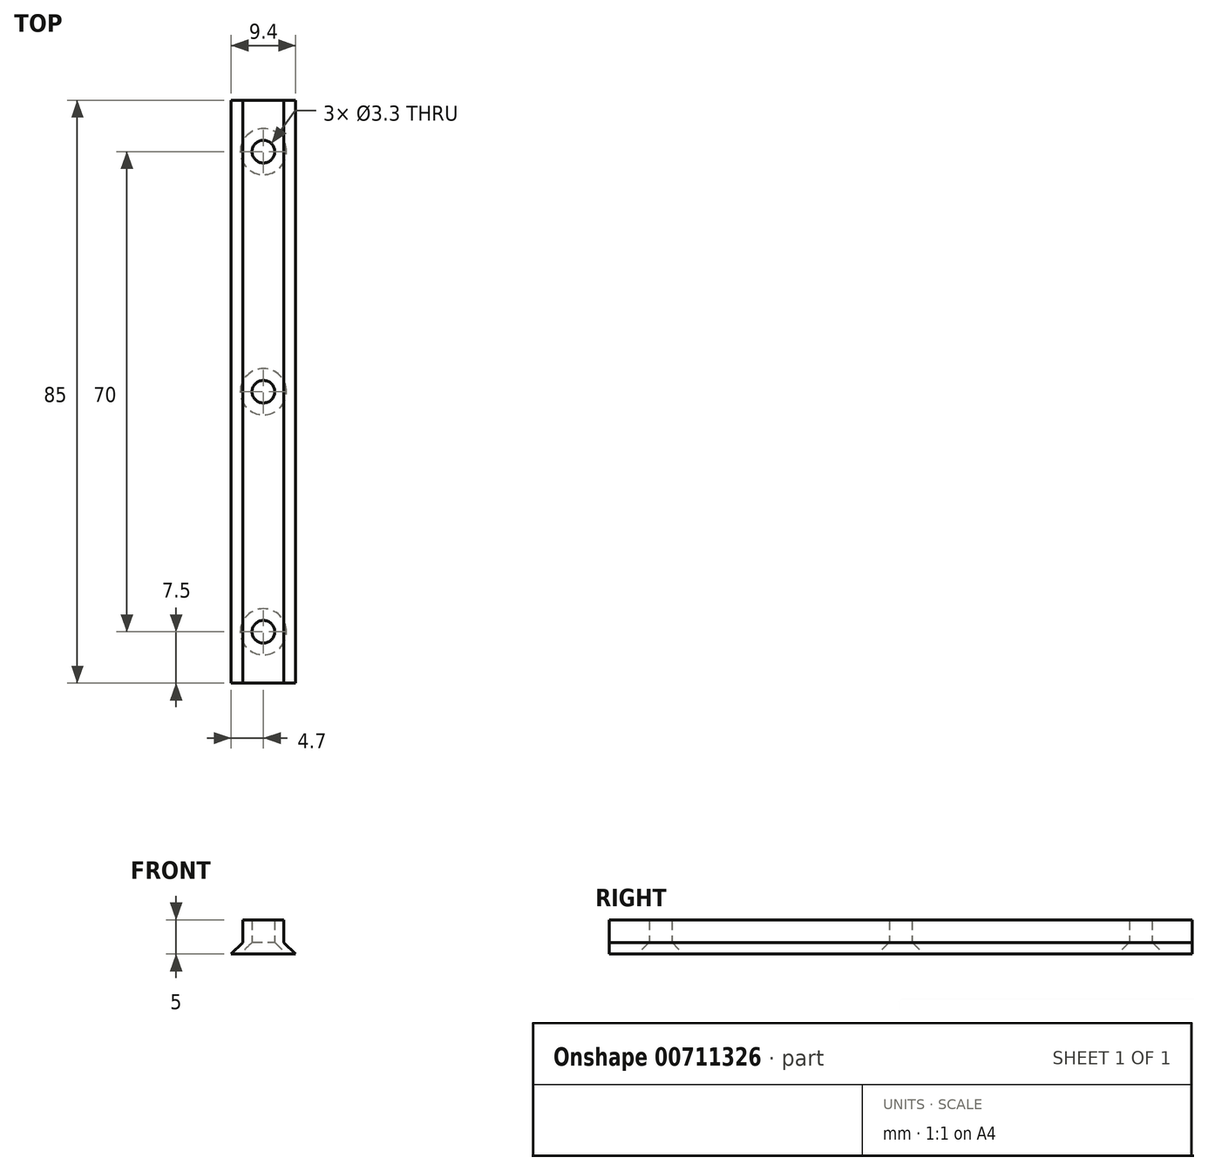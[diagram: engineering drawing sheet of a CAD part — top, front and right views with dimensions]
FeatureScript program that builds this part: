
annotation { "Feature Type Name" : "Feature", "Feature Type Description" : "" }
export const myFeature = defineFeature(function(context is Context, id is Id, definition is map)
    precondition{}
    {
        {
            var Q0;
            Q0=qCreatedBy(makeId("Front.planeOp"),FACE);
            var sketch = newSketch(context, id + "F0", { "sketchPlane" : qUnion([Q0])});
            skLineSegment(sketch, "E0.bottom", {"start": v(3, -1.65) * mm, "end": v(-3, -1.65) * mm});
            skLineSegment(sketch, "E0.top", {"start": v(3, 1.65) * mm, "end": v(-3, 1.65) * mm});
            skLineSegment(sketch, "E0.left", {"start": v(3, -1.65) * mm, "end": v(3, 1.65) * mm});
            skLineSegment(sketch, "E0.right", {"start": v(-3, -1.65) * mm, "end": v(-3, 1.65) * mm});
            skPoint(sketch, "E0.middle", {"position": v(0, 0) * mm});
            skLineSegment(sketch, "E1", {"start": v(-4.7, -3.35) * mm, "end": v(4.7, -3.35) * mm});
            skLineSegment(sketch, "E2", {"start": v(3, -1.65) * mm, "end": v(4.7, -3.35) * mm});
            skLineSegment(sketch, "E3", {"start": v(-3, -1.65) * mm, "end": v(-4.7, -3.35) * mm});
            skSolve(sketch);
        }
        {
            var Q0;
            Q0=makeQuery(id+"F0.imprint","IMPRINT",FACE,{"disambiguationData":[TD([[makeQuery(id+"F0.imprint","IMPRINT",EDGE,{"derivedFrom":sQuery(id+"F0.wireOp",EDGE,"E0.bottom")}),-1.0]])]});
            var Q1;
            Q1=makeQuery(id+"F0.imprint","IMPRINT",FACE,{"disambiguationData":[TD([[makeQuery(id+"F0.imprint","IMPRINT",EDGE,{"derivedFrom":sQuery(id+"F0.wireOp",EDGE,"E0.bottom")}),1.0]])]});
            var Q2;
            Q2=sQuery(id+"F0.wireOp",EDGE,"E3");
            var Q3;
            Q3=sQuery(id+"F0.wireOp",EDGE,"E0.top");
            var Q4;
            Q4=sQuery(id+"F0.wireOp",EDGE,"E2");
            var Q5;
            Q5=sQuery(id+"F0.wireOp",EDGE,"E1");
            var Q6;
            Q6=sQuery(id+"F0.wireOp",EDGE,"E0.right");
            var Q7;
            Q7=sQuery(id+"F0.wireOp",EDGE,"E0.left");
            var Q8;
            Q8=sQuery(id+"F0.wireOp",EDGE,"E0.bottom");
            extrude(context, id + "F1", {"entities" : qUnion([Q0, Q1]), "surfaceEntities" : qUnion([Q2, Q3, Q4, Q5, Q6, Q7, Q8]), "endBound" : BoundingType.SYMMETRIC, "depth" : 85 * mm, "offsetDistance" : 25 * mm});
        }
        {
            var Q0;
            Q0=makeQuery(id+"F1.opExtrude","SWEPT_FACE",FACE,{"disambiguationData":[OSD([sQuery(id+"F0.wireOp",EDGE,"E1")])]});
            var sketch = newSketch(context, id + "F2", { "sketchPlane" : qUnion([Q0])});
            skLineSegment(sketch, "E4", {"start": v(0, 0) * mm, "end": v(0, 35) * mm});
            skLineSegment(sketch, "E5", {"start": v(0, 0) * mm, "end": v(0, -35) * mm});
            skSolve(sketch);
        }
        {
            var Q0;
            Q0=sQuery(id+"F2.wireOp",VERTEX,"E5.start");
            var Q1;
            Q1=sQuery(id+"F2.wireOp",VERTEX,"E4.end");
            var Q2;
            Q2=sQuery(id+"F2.wireOp",VERTEX,"E5.end");
            var Q3;
            Q3=makeQuery(id+"F1.opExtrude","SWEPT_BODY",BODY,{"disambiguationData":[OSD([sQuery(id+"F0.wireOp",EDGE,"E0.top"),sQuery(id+"F0.wireOp",EDGE,"E0.left"),sQuery(id+"F0.wireOp",EDGE,"E0.right"),sQuery(id+"F0.wireOp",EDGE,"E1"),sQuery(id+"F0.wireOp",EDGE,"E2"),sQuery(id+"F0.wireOp",EDGE,"E3")])]});
            hole(context, id + "F3", {"style" : HoleStyle.C_SINK, "endStyle" : HoleEndStyle.THROUGH, "standardTappedOrClearance" : lookupTablePath({ "standard" : "ISO", "fit" : "Normal", "size" : "M3", "type" : "Clearance" }), "standardBlindInLast" : lookupTablePath({ "fit" : "Standard", "standard" : "ISO", "size" : "M3", "type" : "Clearance" }), "holeDiameter" : 3.3 * mm, "cSinkDiameter" : 6.72 * mm, "cSinkAngle" : 90 * degree, "majorDiameter" : 5 * mm, "isTappedThrough" : true, "tappedDepth" : 12 * mm, "tapClearance" : 3, "startFromSketch" : true, "locations" : qUnion([Q0, Q1, Q2]), "scope" : qUnion([Q3])});
        }
    });
